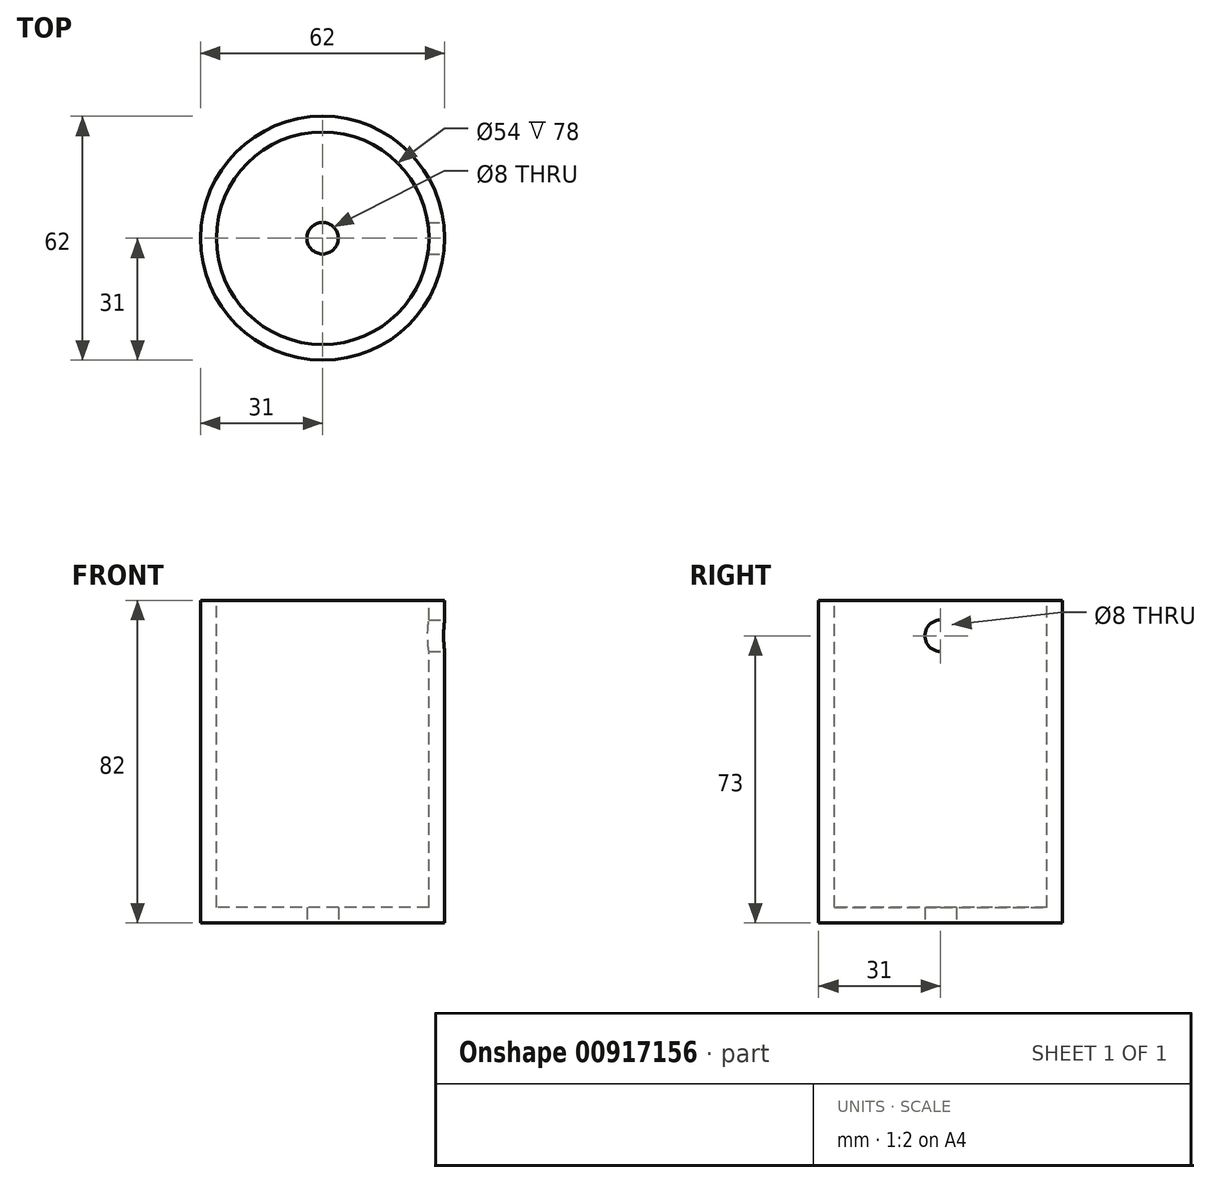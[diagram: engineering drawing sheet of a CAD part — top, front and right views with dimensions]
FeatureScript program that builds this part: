
annotation { "Feature Type Name" : "Feature", "Feature Type Description" : "" }
export const myFeature = defineFeature(function(context is Context, id is Id, definition is map)
    precondition{}
    {
        {
            var Q0;
            Q0=qCreatedBy(makeId("Top.planeOp"),FACE);
            var sketch = newSketch(context, id + "F0", { "sketchPlane" : qUnion([Q0])});
            skCircle(sketch, "E0", {"center": v(0, 0) * mm, "radius": 31 * mm});
            skSolve(sketch);
        }
        {
            var Q0;
            Q0=makeQuery(id+"F0.imprint","IMPRINT",FACE,{"disambiguationData":[TD([[makeQuery(id+"F0.imprint","IMPRINT",EDGE,{"derivedFrom":sQuery(id+"F0.wireOp",EDGE,"E0")}),1.0]])]});
            extrude(context, id + "F1", {"entities" : qUnion([Q0]), "depth" : 82 * mm, "offsetDistance" : 25 * mm});
        }
        {
            var Q0;
            Q0=makeQuery(id+"F1.opExtrude","CAP_FACE",FACE,{"disambiguationData":[OSD([sQuery(id+"F0.wireOp",EDGE,"E0")])],"isStart":false});
            var sketch = newSketch(context, id + "F2", { "sketchPlane" : qUnion([Q0])});
            skCircle(sketch, "E1", {"center": v(0, 0) * mm, "radius": 27 * mm});
            skSolve(sketch);
        }
        {
            var Q0;
            Q0 = qSketchRegion(id + "F2", true);
            extrude(context, id + "F3", {"entities" : qUnion([Q0]), "operationType" : NewBodyOperationType.REMOVE, "oppositeDirection" : true, "depth" : 78 * mm, "offsetDistance" : 25 * mm});
        }
        {
            var Q0;
            Q0=makeQuery(id+"F1.opExtrude","CAP_FACE",FACE,{"disambiguationData":[OSD([sQuery(id+"F0.wireOp",EDGE,"E0")])],"isStart":true});
            var sketch = newSketch(context, id + "F4", { "sketchPlane" : qUnion([Q0])});
            skCircle(sketch, "E2", {"center": v(0, 0) * mm, "radius": 4 * mm});
            skSolve(sketch);
        }
        {
            var Q0;
            Q0 = qSketchRegion(id + "F4", true);
            extrude(context, id + "F5", {"entities" : qUnion([Q0]), "operationType" : NewBodyOperationType.REMOVE, "endBound" : BoundingType.UP_TO_NEXT, "oppositeDirection" : true, "depth" : 25 * mm, "offsetDistance" : 25 * mm});
        }
        {
            var Q0;
            Q0=qCreatedBy(makeId("Right.planeOp"),FACE);
            cPlane(context, id + "F6", {"entities" : qUnion([Q0]), "cplaneType" : CPlaneType.OFFSET, "offset" : 31 * mm, "width" : 150 * mm, "height" : 150 * mm});
        }
        {
            var Q0;
            Q0=qCreatedBy(id+"F6.planeOp",FACE);
            var sketch = newSketch(context, id + "F7", { "sketchPlane" : qUnion([Q0])});
            skCircle(sketch, "E3", {"center": v(0, 73) * mm, "radius": 4 * mm});
            skSolve(sketch);
        }
        {
            var Q0;
            Q0=makeQuery(id+"F7.imprint","IMPRINT",FACE,{"disambiguationData":[TD([[makeQuery(id+"F7.imprint","IMPRINT",EDGE,{"derivedFrom":sQuery(id+"F7.wireOp",EDGE,"E3")}),1.0]])]});
            extrude(context, id + "F8", {"entities" : qUnion([Q0]), "operationType" : NewBodyOperationType.REMOVE, "endBound" : BoundingType.UP_TO_NEXT, "oppositeDirection" : true, "depth" : 25 * mm, "offsetDistance" : 25 * mm});
        }
    });
